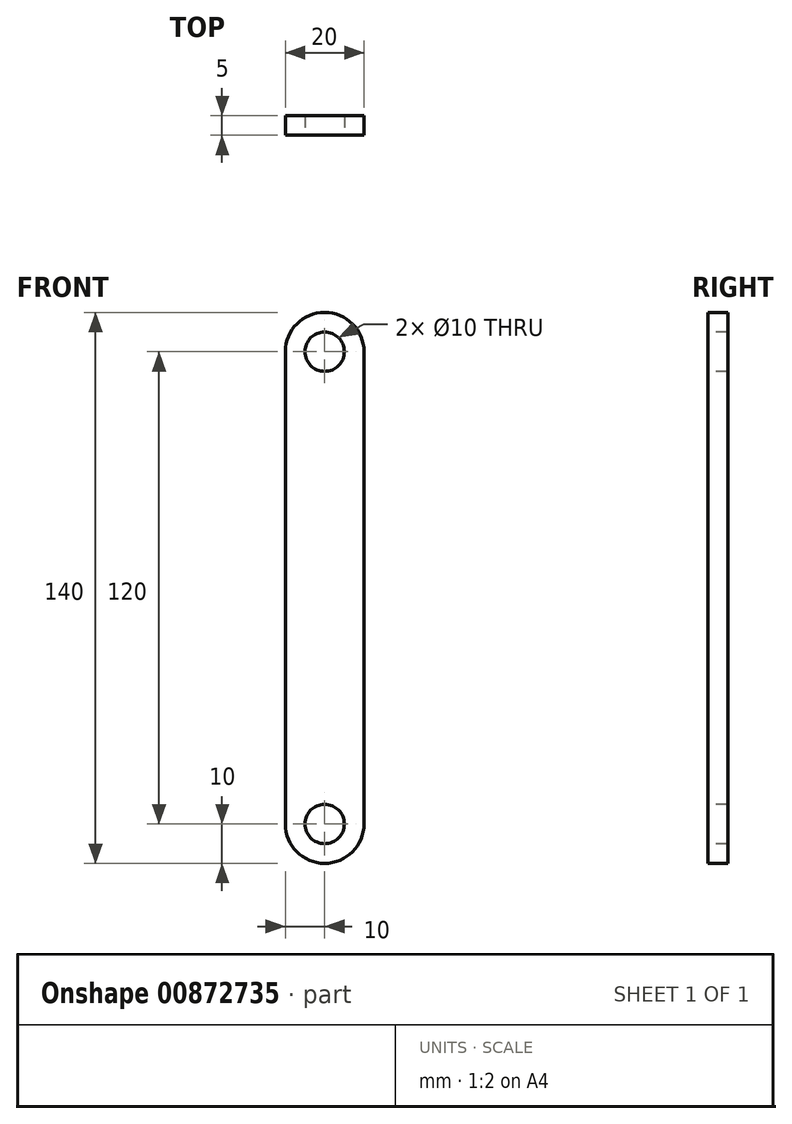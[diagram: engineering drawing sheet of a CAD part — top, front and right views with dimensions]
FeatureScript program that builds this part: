
annotation { "Feature Type Name" : "Feature", "Feature Type Description" : "" }
export const myFeature = defineFeature(function(context is Context, id is Id, definition is map)
    precondition{}
    {
        {
            var Q0;
            Q0=qCreatedBy(makeId("Front.planeOp"),FACE);
            var sketch = newSketch(context, id + "F0", { "sketchPlane" : qUnion([Q0])});
            skCircle(sketch, "E0", {"center": v(0, 60) * mm, "radius": 10 * mm});
            skCircle(sketch, "E1", {"center": v(0, -60) * mm, "radius": 10 * mm});
            skLineSegment(sketch, "E2", {"start": v(10, 60) * mm, "end": v(10, -60) * mm});
            skLineSegment(sketch, "E3", {"start": v(-10, 60) * mm, "end": v(-10, -60) * mm});
            skSolve(sketch);
        }
        {
            var Q0;
            Q0 = qSketchRegion(id + "F0", true);
            extrude(context, id + "F1", {"entities" : qUnion([Q0]), "depth" : 5 * mm, "offsetDistance" : 25 * mm});
        }
        {
            var Q0;
            Q0=makeQuery(id+"F1.opExtrude","CAP_FACE",FACE,{"disambiguationData":[OSD([sQuery(id+"F0.wireOp",EDGE,"E0"),sQuery(id+"F0.wireOp",EDGE,"E1"),sQuery(id+"F0.wireOp",EDGE,"E2"),sQuery(id+"F0.wireOp",EDGE,"E3")])],"isStart":false});
            var sketch = newSketch(context, id + "F2", { "sketchPlane" : qUnion([Q0])});
            skCircle(sketch, "E4", {"center": v(0, 60) * mm, "radius": 5 * mm});
            skCircle(sketch, "E5", {"center": v(0, -60) * mm, "radius": 5 * mm});
            skSolve(sketch);
        }
        {
            var Q0;
            Q0 = qSketchRegion(id + "F2", true);
            extrude(context, id + "F3", {"entities" : qUnion([Q0]), "operationType" : NewBodyOperationType.REMOVE, "oppositeDirection" : true, "depth" : 25 * mm, "offsetDistance" : 25 * mm});
        }
    });
